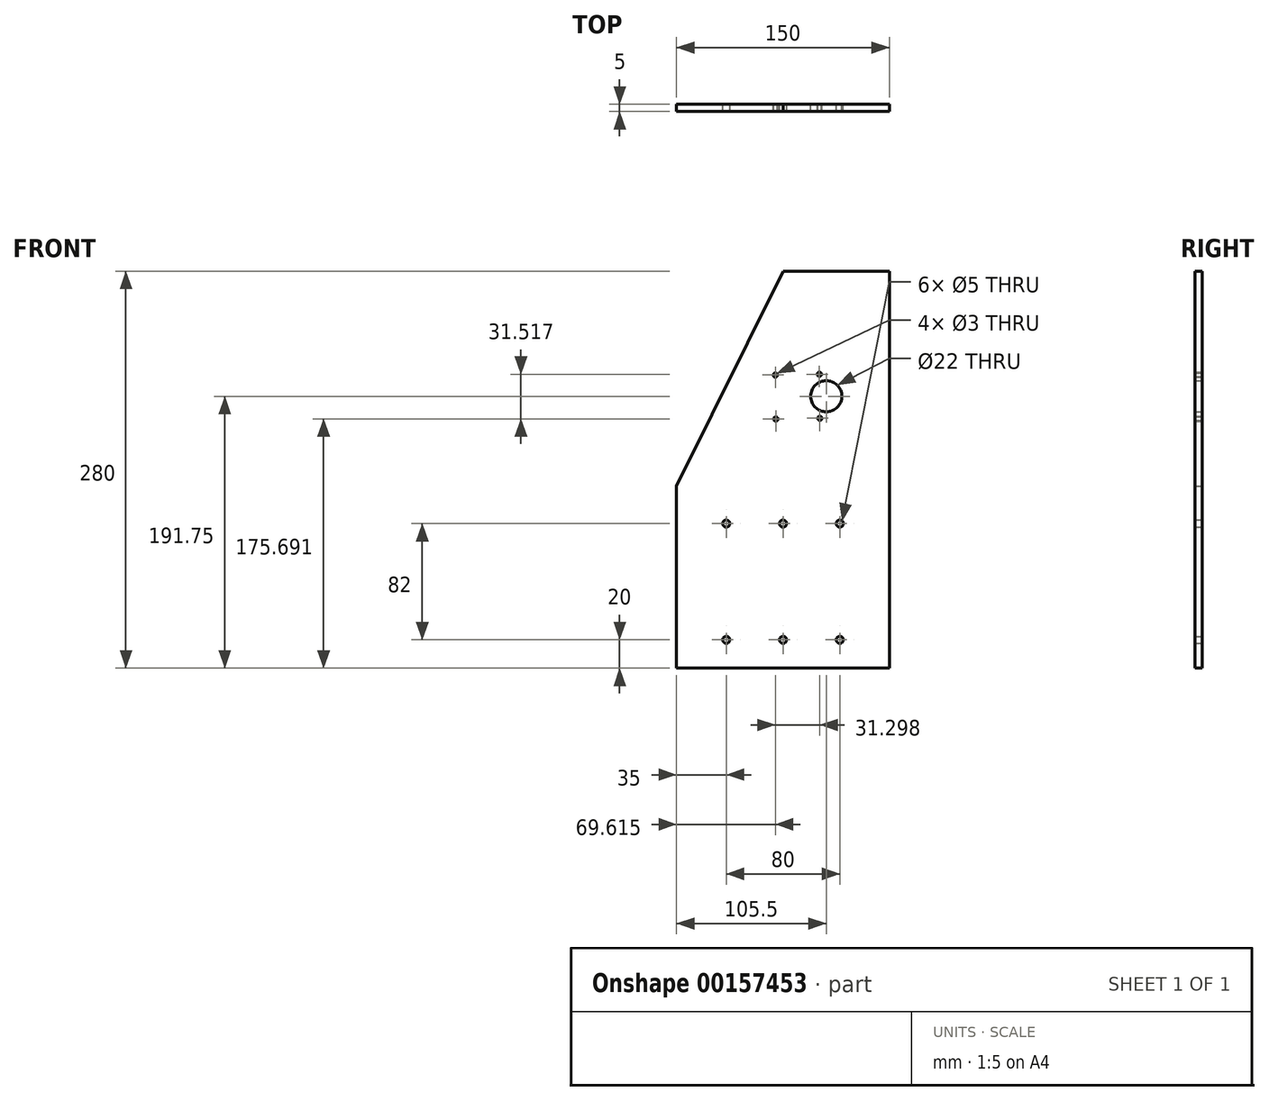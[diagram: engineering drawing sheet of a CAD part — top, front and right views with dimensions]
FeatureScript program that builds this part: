
annotation { "Feature Type Name" : "Feature", "Feature Type Description" : "" }
export const myFeature = defineFeature(function(context is Context, id is Id, definition is map)
    precondition{}
    {
        {
            var Q0;
            Q0=qCreatedBy(makeId("Front.planeOp"),FACE);
            var sketch = newSketch(context, id + "F0", { "sketchPlane" : qUnion([Q0])});
            skLineSegment(sketch, "E0.bottom", {"start": v(75, -140) * mm, "end": v(-75, -140) * mm});
            skLineSegment(sketch, "E0.top", {"start": v(75, 140) * mm, "end": v(0, 140) * mm});
            skLineSegment(sketch, "E0.left", {"start": v(75, -140) * mm, "end": v(75, 140) * mm});
            skLineSegment(sketch, "E0.right", {"start": v(-75, -140) * mm, "end": v(-75, -11.7) * mm});
            skPoint(sketch, "E0.middle", {"position": v(0, 0) * mm});
            skCircle(sketch, "E1", {"center": v(-40, -38) * mm, "radius": 2.5 * mm});
            skCircle(sketch, "E2", {"center": v(0, -38) * mm, "radius": 2.5 * mm});
            skCircle(sketch, "E3", {"center": v(-40, -120) * mm, "radius": 2.5 * mm});
            skCircle(sketch, "E4", {"center": v(0, -120) * mm, "radius": 2.5 * mm});
            skCircle(sketch, "E5", {"center": v(40, -120) * mm, "radius": 2.5 * mm});
            skCircle(sketch, "E6", {"center": v(40, -38) * mm, "radius": 2.5 * mm});
            skLineSegment(sketch, "E7", {"start": v(0, 140) * mm, "end": v(-75, -11.7) * mm});
            skPoint(sketch, "E8.orphan", {"position": v(-75, 140) * mm});
            skCircle(sketch, "E9", {"center": v(30.5, 51.75) * mm, "radius": 11 * mm});
            skCircle(sketch, "E10", {"center": v(-5.38, 66.7) * mm, "radius": 1.5 * mm});
            skCircle(sketch, "E11", {"center": v(25.62, 67.2) * mm, "radius": 1.5 * mm});
            skCircle(sketch, "E12", {"center": v(25.91, 36.2) * mm, "radius": 1.5 * mm});
            skCircle(sketch, "E13", {"center": v(-5.09, 35.7) * mm, "radius": 1.5 * mm});
            skSolve(sketch);
        }
        {
            var Q0;
            Q0=makeQuery(id+"F0.imprint","IMPRINT",FACE,{"disambiguationData":[TD([[makeQuery(id+"F0.imprint","IMPRINT",EDGE,{"derivedFrom":sQuery(id+"F0.wireOp",EDGE,"E0.bottom")}),-1.0]])]});
            extrude(context, id + "F1", {"entities" : qUnion([Q0]), "depth" : 5 * mm});
        }
    });
